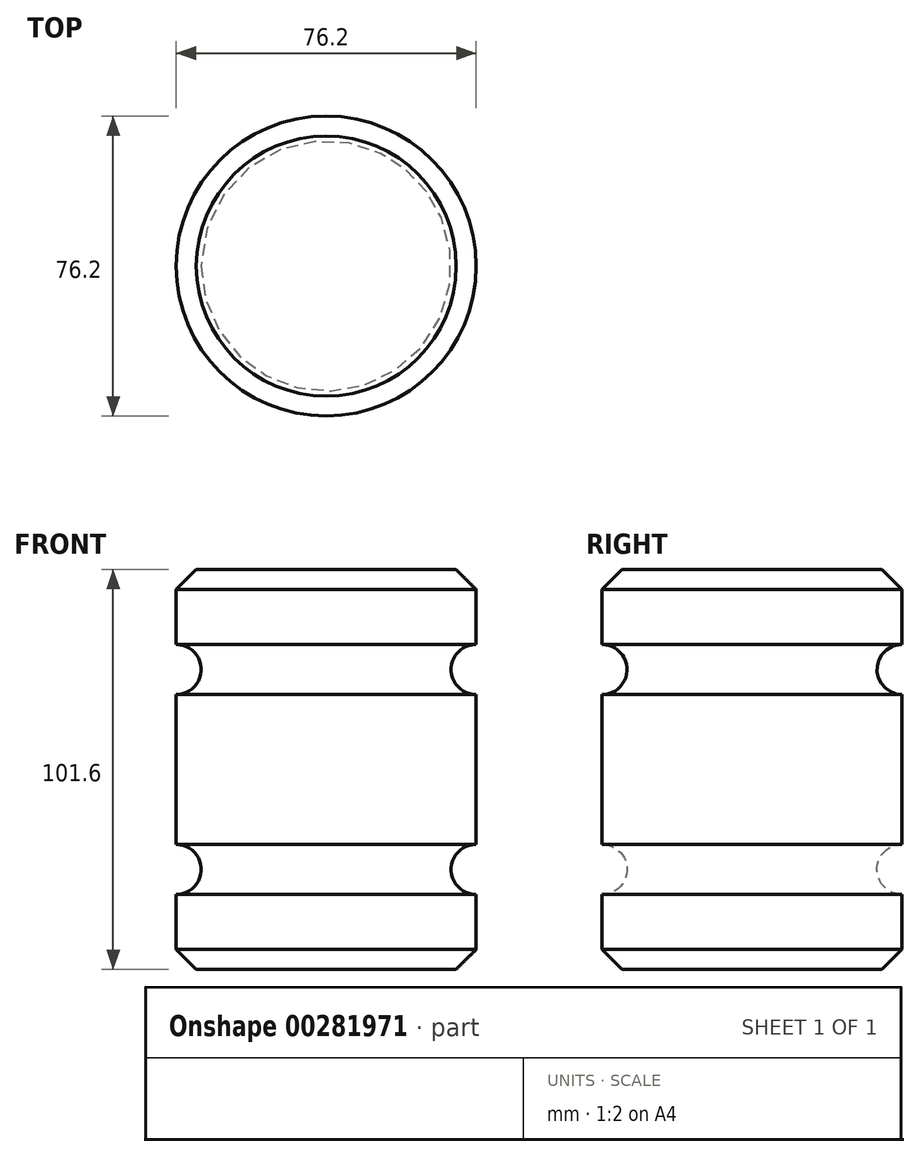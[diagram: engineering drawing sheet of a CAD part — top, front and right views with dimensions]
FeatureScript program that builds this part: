
annotation { "Feature Type Name" : "Feature", "Feature Type Description" : "" }
export const myFeature = defineFeature(function(context is Context, id is Id, definition is map)
    precondition{}
    {
        {
            var Q0;
            Q0=qCreatedBy(makeId("Front.planeOp"),FACE);
            var sketch = newSketch(context, id + "F0", { "sketchPlane" : qUnion([Q0])});
            skLineSegment(sketch, "E0.bottom", {"start": v(0, 0) * mm, "end": v(-38.1, 0) * mm});
            skLineSegment(sketch, "E0.top", {"start": v(0, 101.6) * mm, "end": v(-38.1, 101.6) * mm});
            skLineSegment(sketch, "E0.left", {"start": v(0, 0) * mm, "end": v(0, 19.05) * mm});
            skLineSegment(sketch, "E0.right", {"start": v(-38.1, 0) * mm, "end": v(-38.1, 101.6) * mm});
            skArc(sketch, "E1", {"start": v(0, 82.55) * mm, "mid": v(-6.35, 76.2) * mm, "end": v(0, 69.85) * mm});
            skArc(sketch, "E2", {"start": v(0, 31.75) * mm, "mid": v(-6.35, 25.4) * mm, "end": v(0, 19.05) * mm});
            skLineSegment(sketch, "E3.trimOffspring", {"start": v(0, 82.55) * mm, "end": v(0, 101.6) * mm});
            skLineSegment(sketch, "E4.trimOffspring", {"start": v(0, 31.75) * mm, "end": v(0, 69.85) * mm});
            skSolve(sketch);
        }
        {
            var Q0;
            Q0 = qSketchRegion(id + "F0", true);
            var Q1;
            Q1=sQuery(id+"F0.wireOp",EDGE,"E0.right");
            revolve(context, id + "F1", {"entities" : qUnion([Q0]), "axis" : qUnion([Q1]), "revolveType" : RevolveType.FULL});
        }
        {
            var Q0;
            Q0=makeQuery(id+"F1.opRevolve","SWEPT_FACE",FACE,{"disambiguationData":[OSD([sQuery(id+"F0.wireOp",EDGE,"E0.bottom")])]});
            chamfer(context, id + "F2", {"entities" : qUnion([Q0]), "width" : 5.08 * mm, "tangentPropagation" : true});
        }
        {
            var Q0;
            Q0=makeQuery(id+"F1.opRevolve","SWEPT_FACE",FACE,{"disambiguationData":[OSD([sQuery(id+"F0.wireOp",EDGE,"E0.top")])]});
            chamfer(context, id + "F3", {"entities" : qUnion([Q0]), "width" : 5.08 * mm, "tangentPropagation" : true});
        }
    });
